# Revit family: Haworth_BeHold-Element_FlowerPlanter_EU_PRELIMINARY
name_source: partatom
category: Furniture
units: mm (PartAtom-declared; Revit-internal decimal feet)

## family parameters
Always vertical = Yes
Cut with Voids When Loaded = No
OmniClass Number = 23.40.70.14.64.21
OmniClass Title = Systems Furniture
Room Calculation Point = No
Shared = No
Work Plane-Based = No

## types (6) — shared parameters
Actual Depth = 43 cm
Assembly Code = E2020200
Custom Size = No
Description = Haworth - BeHold Design - Flower Planter
Manufacturer = Haworth
Max. Width = 160 cm
Min. Width = 50 cm
Model = ESGFB
Revision Number = 1
Size = Verify Final Dim. w/ Haworth
URL = https://www.haworth.com
URL - Product = https://www.haworth.com
Warranty = http://www.haworth.com

## per-type parameters (varying)
| type | Actual Height | Actual Width | High | Large | Low | Width |
| 120w x 43.3d | 37 cm | 120 cm | Yes | Yes | No | 120 cm |
| 100w x 43.3d | 37 cm | 100 cm | Yes | Yes | No | 100 cm |
| 160w x 43.3d | 37 cm | 160 cm | Yes | Yes | No | 160 cm |
| 50w x 43.3d | 25 cm | 50 cm | No | No | Yes | 50 cm |
| 60w x 43.3d | 37 cm | 60 cm | Yes | No | No | 60 cm |
| 80w x 43.3d | 25 cm | 80 cm | No | No | Yes | 80 cm |

## geometry (parser evidence)
native form markers: Sweep x2
no freeform markers — native parametric forms only
